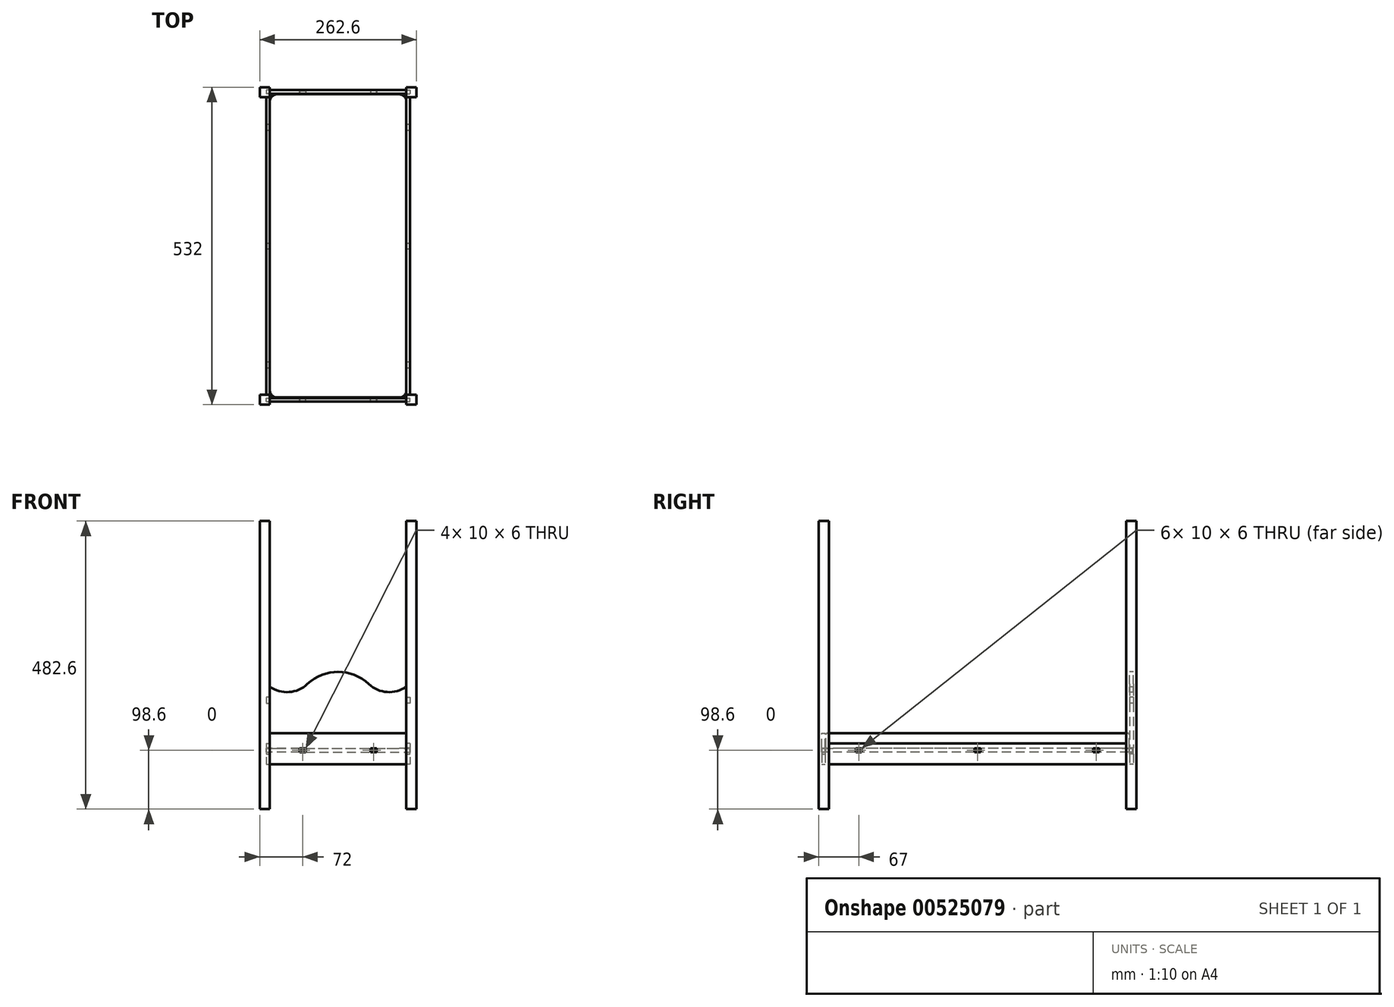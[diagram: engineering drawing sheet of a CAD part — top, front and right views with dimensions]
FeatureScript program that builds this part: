
annotation { "Feature Type Name" : "Feature", "Feature Type Description" : "" }
export const myFeature = defineFeature(function(context is Context, id is Id, definition is map)
    precondition{}
    {
        {
            var Q0;
            Q0=qCreatedBy(makeId("Top.planeOp"),FACE);
            cPlane(context, id + "F0", {"entities" : qUnion([Q0]), "cplaneType" : CPlaneType.OFFSET, "offset" : (5 * 25.4) * mm, "width" : 150 * mm, "height" : 150 * mm});
        }
        {
            var Q0;
            Q0=qCreatedBy(makeId("Top.planeOp"),FACE);
            cPlane(context, id + "F1", {"entities" : qUnion([Q0]), "cplaneType" : CPlaneType.OFFSET, "offset" : (4 * 25.4) * mm, "width" : 150 * mm, "height" : 150 * mm});
        }
        {
            var Q0;
            Q0=qCreatedBy(id+"F0.planeOp",FACE);
            var sketch = newSketch(context, id + "F2", { "sketchPlane" : qUnion([Q0])});
            skLineSegment(sketch, "E0.bottom", {"start": v(-114.3, 254) * mm, "end": v(114.3, 254) * mm});
            skLineSegment(sketch, "E0.top", {"start": v(-114.3, -254) * mm, "end": v(114.3, -254) * mm});
            skLineSegment(sketch, "E0.left", {"start": v(-114.3, 254) * mm, "end": v(-114.3, -254) * mm});
            skLineSegment(sketch, "E0.right", {"start": v(114.3, 254) * mm, "end": v(114.3, -254) * mm});
            skLineSegment(sketch, "E1", {"start": v(0, 66.41) * mm, "end": v(0, 0) * mm, "construction": true});
            skLineSegment(sketch, "E2", {"start": v(0, 0) * mm, "end": v(28.07, 0) * mm, "construction": true});
            skSolve(sketch);
        }
        {
            var Q0;
            Q0=qCreatedBy(id+"F1.planeOp",FACE);
            var sketch = newSketch(context, id + "F3", { "sketchPlane" : qUnion([Q0])});
            skLineSegment(sketch, "E3.0.0", {"start": v(-114.3, 254) * mm, "end": v(-114.3, 204) * mm});
            skLineSegment(sketch, "E3.0.1", {"start": v(-114.3, -254) * mm, "end": v(-64.3, -254) * mm});
            skLineSegment(sketch, "E3.0.2", {"start": v(114.3, -254) * mm, "end": v(114.3, -204) * mm});
            skLineSegment(sketch, "E3.0.3", {"start": v(114.3, 254) * mm, "end": v(64.3, 254) * mm});
            skLineSegment(sketch, "E4.0", {"start": v(0, 66.41) * mm, "end": v(0, 0) * mm, "construction": true});
            skPoint(sketch, "E5.0", {"position": v(14.03, 0) * mm});
            skLineSegment(sketch, "E6.bottom", {"start": v(-120.3, 5) * mm, "end": v(-114.3, 5) * mm});
            skLineSegment(sketch, "E6.top", {"start": v(-120.3, -5) * mm, "end": v(-114.3, -5) * mm});
            skLineSegment(sketch, "E6.left", {"start": v(-120.3, 5) * mm, "end": v(-120.3, -5) * mm});
            skLineSegment(sketch, "E6.right", {"start": v(120.3, 5) * mm, "end": v(120.3, -5) * mm});
            skPoint(sketch, "E7.0", {"position": v(14.03, 192.46) * mm});
            skLineSegment(sketch, "E8.bottom", {"start": v(-120.3, 204) * mm, "end": v(-114.3, 204) * mm});
            skLineSegment(sketch, "E8.top", {"start": v(-120.3, 194) * mm, "end": v(-114.3, 194) * mm});
            skLineSegment(sketch, "E8.left", {"start": v(-120.3, 204) * mm, "end": v(-120.3, 194) * mm});
            skLineSegment(sketch, "E8.right", {"start": v(120.3, 204) * mm, "end": v(120.3, 194) * mm});
            skLineSegment(sketch, "E9.MirrorCS", {"start": v(120.3, -204) * mm, "end": v(120.3, -194) * mm});
            skLineSegment(sketch, "E10.MirrorCS", {"start": v(-120.3, -204) * mm, "end": v(-120.3, -194) * mm});
            skLineSegment(sketch, "E11.MirrorCS", {"start": v(-120.3, -204) * mm, "end": v(-114.3, -204) * mm});
            skLineSegment(sketch, "E12.MirrorCS", {"start": v(-120.3, -194) * mm, "end": v(-114.3, -194) * mm});
            skPoint(sketch, "E13.MirrorP", {"position": v(14.03, -192.46) * mm});
            skLineSegment(sketch, "E14.trimOffspring", {"start": v(114.3, 204) * mm, "end": v(120.3, 204) * mm});
            skLineSegment(sketch, "E15.trimOffspring", {"start": v(114.3, 194) * mm, "end": v(120.3, 194) * mm});
            skLineSegment(sketch, "E16.trimOffspring", {"start": v(114.3, 5) * mm, "end": v(120.3, 5) * mm});
            skLineSegment(sketch, "E17.trimOffspring", {"start": v(114.3, -5) * mm, "end": v(120.3, -5) * mm});
            skLineSegment(sketch, "E18.trimOffspring", {"start": v(114.3, 5) * mm, "end": v(114.3, 194) * mm});
            skLineSegment(sketch, "E19.trimOffspring", {"start": v(-114.3, -5) * mm, "end": v(-114.3, -194) * mm});
            skLineSegment(sketch, "E20.trimOffspring", {"start": v(-114.3, 194) * mm, "end": v(-114.3, 5) * mm});
            skLineSegment(sketch, "E21.trimOffspring", {"start": v(114.3, 204) * mm, "end": v(114.3, 254) * mm});
            skLineSegment(sketch, "E22.trimOffspring", {"start": v(114.3, -194) * mm, "end": v(120.3, -194) * mm});
            skLineSegment(sketch, "E23.trimOffspring", {"start": v(114.3, -204) * mm, "end": v(120.3, -204) * mm});
            skLineSegment(sketch, "E24.trimOffspring", {"start": v(-114.3, -204) * mm, "end": v(-114.3, -254) * mm});
            skLineSegment(sketch, "E25.trimOffspring", {"start": v(114.3, -194) * mm, "end": v(114.3, -5) * mm});
            skLineSegment(sketch, "E26", {"start": v(-64.3, 254) * mm, "end": v(-64.3, 260) * mm});
            skLineSegment(sketch, "E27", {"start": v(-64.3, 260) * mm, "end": v(-54.3, 260) * mm});
            skLineSegment(sketch, "E28", {"start": v(-54.3, 260) * mm, "end": v(-54.3, 254) * mm});
            skLineSegment(sketch, "E29", {"start": v(64.3, 254) * mm, "end": v(64.3, 260) * mm});
            skLineSegment(sketch, "E30", {"start": v(64.3, 260) * mm, "end": v(54.3, 260) * mm});
            skLineSegment(sketch, "E31", {"start": v(54.3, 260) * mm, "end": v(54.3, 254) * mm});
            skLineSegment(sketch, "E32.trimOffspring", {"start": v(-64.3, 254) * mm, "end": v(-114.3, 254) * mm});
            skLineSegment(sketch, "E33.trimOffspring", {"start": v(54.3, 254) * mm, "end": v(-54.3, 254) * mm});
            skLineSegment(sketch, "E34.MirrorCS", {"start": v(-64.3, -254) * mm, "end": v(-64.3, -260) * mm});
            skLineSegment(sketch, "E35.MirrorCS", {"start": v(-54.3, -260) * mm, "end": v(-54.3, -254) * mm});
            skLineSegment(sketch, "E36.MirrorCS", {"start": v(64.3, -254) * mm, "end": v(64.3, -260) * mm});
            skLineSegment(sketch, "E37.MirrorCS", {"start": v(54.3, -260) * mm, "end": v(54.3, -254) * mm});
            skLineSegment(sketch, "E38.MirrorCS", {"start": v(64.3, -260) * mm, "end": v(54.3, -260) * mm});
            skLineSegment(sketch, "E39.MirrorCS", {"start": v(-64.3, -260) * mm, "end": v(-54.3, -260) * mm});
            skLineSegment(sketch, "E40.trimOffspring", {"start": v(-54.3, -254) * mm, "end": v(54.3, -254) * mm});
            skLineSegment(sketch, "E41.trimOffspring", {"start": v(64.3, -254) * mm, "end": v(114.3, -254) * mm});
            skSolve(sketch);
        }
        {
            var Q0;
            Q0=makeQuery(id+"F3.imprint","IMPRINT",FACE,{"disambiguationData":[TD([[makeQuery(id+"F3.imprint","IMPRINT",EDGE,{"derivedFrom":sQuery(id+"F3.wireOp",EDGE,"E3.0.0")}),1.0]])]});
            extrude(context, id + "F4", {"entities" : qUnion([Q0]), "oppositeDirection" : true, "depth" : 6 * mm, "offsetDistance" : 25 * mm});
        }
        {
            var Q0;
            Q0=makeQuery(id+"F2.imprint","IMPRINT",FACE,{"disambiguationData":[TD([[makeQuery(id+"F2.imprint","IMPRINT",EDGE,{"derivedFrom":sQuery(id+"F2.wireOp",EDGE,"E0.bottom")}),-1.0]])]});
            extrude(context, id + "F5", {"entities" : qUnion([Q0]), "oppositeDirection" : true, "depth" : 25 * mm, "offsetDistance" : 25 * mm});
        }
        {
            var Q0;
            Q0=makeQuery(id+"F5.opExtrude","SWEPT_EDGE",EDGE,{"disambiguationData":[OSD([sQuery(id+"F2.wireOp",EDGE,"E0.bottom"),sQuery(id+"F2.wireOp",EDGE,"E0.left")])]});
            var Q1;
            Q1=makeQuery(id+"F5.opExtrude","SWEPT_EDGE",EDGE,{"disambiguationData":[OSD([sQuery(id+"F2.wireOp",EDGE,"E0.top"),sQuery(id+"F2.wireOp",EDGE,"E0.left")])]});
            var Q2;
            Q2=makeQuery(id+"F5.opExtrude","SWEPT_EDGE",EDGE,{"disambiguationData":[OSD([sQuery(id+"F2.wireOp",EDGE,"E0.top"),sQuery(id+"F2.wireOp",EDGE,"E0.right")])]});
            var Q3;
            Q3=makeQuery(id+"F5.opExtrude","SWEPT_EDGE",EDGE,{"disambiguationData":[OSD([sQuery(id+"F2.wireOp",EDGE,"E0.bottom"),sQuery(id+"F2.wireOp",EDGE,"E0.right")])]});
            fillet(context, id + "F6", {"entities" : qUnion([Q0, Q1, Q2, Q3]), "radius" : 12 * mm, "tangentPropagation" : true, "allowEdgeOverflow" : false});
        }
        {
            var Q0;
            Q0=makeQuery(id+"F5.opExtrude","CAP_EDGE",EDGE,{"disambiguationData":[OSD([sQuery(id+"F2.wireOp",EDGE,"E0.right")])],"isStart":true});
            var Q1;
            Q1=makeQuery(id+"F5.opExtrude","CAP_EDGE",EDGE,{"disambiguationData":[OSD([sQuery(id+"F2.wireOp",EDGE,"E0.right")])],"isStart":false});
            fillet(context, id + "F7", {"entities" : qUnion([Q0, Q1]), "radius" : 2 * mm, "tangentPropagation" : true, "allowEdgeOverflow" : false});
        }
        {
            var Q0;
            Q0=qCreatedBy(makeId("Front.planeOp"),FACE);
            cPlane(context, id + "F8", {"entities" : qUnion([Q0]), "cplaneType" : CPlaneType.OFFSET, "offset" : 255 * mm, "oppositeDirection" : true, "width" : 150 * mm, "height" : 150 * mm});
        }
        {
            var Q0;
            Q0=qCreatedBy(id+"F8.planeOp",FACE);
            var sketch = newSketch(context, id + "F9", { "sketchPlane" : qUnion([Q0])});
            skLineSegment(sketch, "E42.top", {"start": v(114.3, 75) * mm, "end": v(-114.3, 75) * mm});
            skLineSegment(sketch, "E42.left", {"start": v(114.3, 205) * mm, "end": v(114.3, 187.5) * mm});
            skLineSegment(sketch, "E42.right", {"start": v(-114.3, 205) * mm, "end": v(-114.3, 187.5) * mm});
            skArc(sketch, "E43", {"start": v(51.41, 209.6) * mm, "mid": v(0, 230) * mm, "end": v(-51.41, 209.6) * mm});
            skArc(sketch, "E44", {"start": v(51.41, 209.6) * mm, "mid": v(82.04, 196.14) * mm, "end": v(114.3, 205) * mm});
            skArc(sketch, "E45.MirrorCS", {"start": v(-51.41, 209.6) * mm, "mid": v(-82.04, 196.14) * mm, "end": v(-114.3, 205) * mm});
            skLineSegment(sketch, "E46", {"start": v(51.46, 230) * mm, "end": v(-51.46, 230) * mm, "construction": true});
            skPoint(sketch, "E46.endSnap0", {"position": v(0, 230) * mm});
            skLineSegment(sketch, "E47", {"start": v(114.3, 140) * mm, "end": v(-114.3, 140) * mm, "construction": true});
            skLineSegment(sketch, "E48", {"start": v(114.3, 187.5) * mm, "end": v(120.3, 187.5) * mm});
            skLineSegment(sketch, "E49", {"start": v(120.3, 187.5) * mm, "end": v(120.3, 177.5) * mm});
            skLineSegment(sketch, "E50", {"start": v(120.3, 177.5) * mm, "end": v(114.3, 177.5) * mm});
            skLineSegment(sketch, "E51.MirrorCS", {"start": v(-120.3, 177.5) * mm, "end": v(-114.3, 177.5) * mm});
            skLineSegment(sketch, "E52.MirrorCS", {"start": v(-120.3, 187.5) * mm, "end": v(-120.3, 177.5) * mm});
            skLineSegment(sketch, "E53.MirrorCS", {"start": v(-114.3, 187.5) * mm, "end": v(-120.3, 187.5) * mm});
            skLineSegment(sketch, "E54.MirrorCS", {"start": v(-114.3, 92.5) * mm, "end": v(-120.3, 92.5) * mm});
            skLineSegment(sketch, "E55.MirrorCS", {"start": v(-120.3, 92.5) * mm, "end": v(-120.3, 102.5) * mm});
            skLineSegment(sketch, "E56.MirrorCS", {"start": v(-120.3, 102.5) * mm, "end": v(-114.3, 102.5) * mm});
            skLineSegment(sketch, "E57.MirrorCS", {"start": v(114.3, 92.5) * mm, "end": v(120.3, 92.5) * mm});
            skLineSegment(sketch, "E58.MirrorCS", {"start": v(120.3, 102.5) * mm, "end": v(114.3, 102.5) * mm});
            skLineSegment(sketch, "E59.MirrorCS", {"start": v(120.3, 92.5) * mm, "end": v(120.3, 102.5) * mm});
            skLineSegment(sketch, "E60.trimOffspring", {"start": v(114.3, 177.5) * mm, "end": v(114.3, 102.5) * mm});
            skLineSegment(sketch, "E61.trimOffspring", {"start": v(-114.3, 177.5) * mm, "end": v(-114.3, 102.5) * mm});
            skLineSegment(sketch, "E62.trimOffspring", {"start": v(-114.3, 92.5) * mm, "end": v(-114.3, 75) * mm});
            skLineSegment(sketch, "E63.trimOffspring", {"start": v(114.3, 92.5) * mm, "end": v(114.3, 75) * mm});
            skLineSegment(sketch, "E64.0.0", {"start": v(54.3, 101.6) * mm, "end": v(64.3, 101.6) * mm});
            skLineSegment(sketch, "E64.0.1", {"start": v(64.3, 101.6) * mm, "end": v(64.3, 95.6) * mm});
            skLineSegment(sketch, "E64.0.2", {"start": v(64.3, 95.6) * mm, "end": v(54.3, 95.6) * mm});
            skLineSegment(sketch, "E64.0.3", {"start": v(54.3, 95.6) * mm, "end": v(54.3, 101.6) * mm});
            skLineSegment(sketch, "E65.0.0", {"start": v(-64.3, 101.6) * mm, "end": v(-54.3, 101.6) * mm});
            skLineSegment(sketch, "E65.0.1", {"start": v(-54.3, 101.6) * mm, "end": v(-54.3, 95.6) * mm});
            skLineSegment(sketch, "E65.0.2", {"start": v(-54.3, 95.6) * mm, "end": v(-64.3, 95.6) * mm});
            skLineSegment(sketch, "E65.0.3", {"start": v(-64.3, 95.6) * mm, "end": v(-64.3, 101.6) * mm});
            skSolve(sketch);
        }
        {
            var Q0;
            Q0 = qSketchRegion(id + "F9", true);
            extrude(context, id + "F10", {"entities" : qUnion([Q0]), "oppositeDirection" : true, "depth" : 6 * mm, "offsetDistance" : 25 * mm});
        }
        {
            var Q0;
            Q0=qCreatedBy(makeId("Front.planeOp"),FACE);
            cPlane(context, id + "F11", {"entities" : qUnion([Q0]), "cplaneType" : CPlaneType.OFFSET, "offset" : 255 * mm, "width" : 150 * mm, "height" : 150 * mm});
        }
        {
            var Q0;
            Q0=qCreatedBy(id+"F11.planeOp",FACE);
            var sketch = newSketch(context, id + "F12", { "sketchPlane" : qUnion([Q0])});
            skLineSegment(sketch, "E66.0", {"start": v(-114.3, 92.5) * mm, "end": v(-114.3, 75) * mm});
            skLineSegment(sketch, "E67", {"start": v(-114.3, 127.27) * mm, "end": v(114.3, 127.27) * mm});
            skLineSegment(sketch, "E68.0.10", {"start": v(-114.3, 102.5) * mm, "end": v(-120.3, 102.5) * mm});
            skLineSegment(sketch, "E68.0.11", {"start": v(-120.3, 102.5) * mm, "end": v(-120.3, 92.5) * mm});
            skLineSegment(sketch, "E68.0.12", {"start": v(-120.3, 92.5) * mm, "end": v(-114.3, 92.5) * mm});
            skLineSegment(sketch, "E68.0.14", {"start": v(-114.3, 75) * mm, "end": v(114.3, 75) * mm});
            skLineSegment(sketch, "E68.0.15", {"start": v(114.3, 75) * mm, "end": v(114.3, 92.5) * mm});
            skLineSegment(sketch, "E68.0.16", {"start": v(114.3, 92.5) * mm, "end": v(120.3, 92.5) * mm});
            skLineSegment(sketch, "E68.0.17", {"start": v(120.3, 92.5) * mm, "end": v(120.3, 102.5) * mm});
            skLineSegment(sketch, "E68.0.18", {"start": v(120.3, 102.5) * mm, "end": v(114.3, 102.5) * mm});
            skLineSegment(sketch, "E68.0.19", {"start": v(114.3, 102.5) * mm, "end": v(114.3, 127.27) * mm});
            skLineSegment(sketch, "E69.0", {"start": v(-114.3, 127.27) * mm, "end": v(-114.3, 102.5) * mm});
            skPoint(sketch, "E70.orphan", {"position": v(-114.3, 177.5) * mm});
            skLineSegment(sketch, "E71.0.0", {"start": v(-54.3, 101.6) * mm, "end": v(-64.3, 101.6) * mm});
            skLineSegment(sketch, "E71.0.1", {"start": v(-64.3, 101.6) * mm, "end": v(-64.3, 95.6) * mm});
            skLineSegment(sketch, "E71.0.2", {"start": v(-64.3, 95.6) * mm, "end": v(-54.3, 95.6) * mm});
            skLineSegment(sketch, "E71.0.3", {"start": v(-54.3, 95.6) * mm, "end": v(-54.3, 101.6) * mm});
            skLineSegment(sketch, "E72.0.0", {"start": v(64.3, 101.6) * mm, "end": v(54.3, 101.6) * mm});
            skLineSegment(sketch, "E72.0.1", {"start": v(54.3, 101.6) * mm, "end": v(54.3, 95.6) * mm});
            skLineSegment(sketch, "E72.0.2", {"start": v(54.3, 95.6) * mm, "end": v(64.3, 95.6) * mm});
            skLineSegment(sketch, "E72.0.3", {"start": v(64.3, 95.6) * mm, "end": v(64.3, 101.6) * mm});
            skSolve(sketch);
        }
        {
            var Q0;
            Q0 = qSketchRegion(id + "F12", true);
            extrude(context, id + "F13", {"entities" : qUnion([Q0]), "depth" : 6 * mm, "offsetDistance" : 25 * mm});
        }
        {
            var Q0;
            Q0=qCreatedBy(makeId("Right.planeOp"),FACE);
            cPlane(context, id + "F14", {"entities" : qUnion([Q0]), "cplaneType" : CPlaneType.OFFSET, "offset" : (4.5 * 25.4) * mm, "oppositeDirection" : true, "width" : 150 * mm, "height" : 150 * mm});
        }
        {
            var Q0;
            Q0=qCreatedBy(id+"F14.planeOp",FACE);
            var sketch = newSketch(context, id + "F15", { "sketchPlane" : qUnion([Q0])});
            skLineSegment(sketch, "E73", {"start": v(249, 110) * mm, "end": v(-249, 110) * mm});
            skLineSegment(sketch, "E74.0", {"start": v(249, 75) * mm, "end": v(-249, 75) * mm});
            skLineSegment(sketch, "E75.0.0", {"start": v(-204, 101.6) * mm, "end": v(-194, 101.6) * mm});
            skLineSegment(sketch, "E75.0.1", {"start": v(-194, 101.6) * mm, "end": v(-194, 95.6) * mm});
            skLineSegment(sketch, "E75.0.2", {"start": v(-194, 95.6) * mm, "end": v(-204, 95.6) * mm});
            skLineSegment(sketch, "E75.0.3", {"start": v(-204, 95.6) * mm, "end": v(-204, 101.6) * mm});
            skLineSegment(sketch, "E76.0.0", {"start": v(-5, 101.6) * mm, "end": v(5, 101.6) * mm});
            skLineSegment(sketch, "E76.0.1", {"start": v(5, 101.6) * mm, "end": v(5, 95.6) * mm});
            skLineSegment(sketch, "E76.0.2", {"start": v(5, 95.6) * mm, "end": v(-5, 95.6) * mm});
            skLineSegment(sketch, "E76.0.3", {"start": v(-5, 95.6) * mm, "end": v(-5, 101.6) * mm});
            skLineSegment(sketch, "E77.0.0", {"start": v(194, 101.6) * mm, "end": v(204, 101.6) * mm});
            skLineSegment(sketch, "E77.0.1", {"start": v(204, 101.6) * mm, "end": v(204, 95.6) * mm});
            skLineSegment(sketch, "E77.0.2", {"start": v(204, 95.6) * mm, "end": v(194, 95.6) * mm});
            skLineSegment(sketch, "E77.0.3", {"start": v(194, 95.6) * mm, "end": v(194, 101.6) * mm});
            skLineSegment(sketch, "E78", {"start": v(-249, 110) * mm, "end": v(-249, 75) * mm});
            skPoint(sketch, "E79.0.end.orphan", {"position": v(-261, 75) * mm});
            skLineSegment(sketch, "E80", {"start": v(249, 110) * mm, "end": v(249, 75) * mm});
            skPoint(sketch, "E81.orphan", {"position": v(261, 75) * mm});
            skSolve(sketch);
        }
        {
            var Q0;
            Q0 = qSketchRegion(id + "F15", true);
            extrude(context, id + "F16", {"entities" : qUnion([Q0]), "oppositeDirection" : true, "depth" : 6 * mm, "offsetDistance" : 25 * mm});
        }
        {
            var Q0;
            Q0=makeQuery(id+"F16.opExtrude","SWEPT_BODY",BODY,{"disambiguationData":[OSD([sQuery(id+"F15.wireOp",EDGE,"E73"),sQuery(id+"F15.wireOp",EDGE,"3c840a2c-036b-4376-a69c-f623c423800d.0"),sQuery(id+"F15.wireOp",EDGE,"E74.0"),sQuery(id+"F15.wireOp",EDGE,"E75.0.0"),sQuery(id+"F15.wireOp",EDGE,"E75.0.1"),sQuery(id+"F15.wireOp",EDGE,"E75.0.2"),sQuery(id+"F15.wireOp",EDGE,"E75.0.3"),sQuery(id+"F15.wireOp",EDGE,"E76.0.0"),sQuery(id+"F15.wireOp",EDGE,"E76.0.1"),sQuery(id+"F15.wireOp",EDGE,"E76.0.2"),sQuery(id+"F15.wireOp",EDGE,"E76.0.3"),sQuery(id+"F15.wireOp",EDGE,"E77.0.0"),sQuery(id+"F15.wireOp",EDGE,"E77.0.1"),sQuery(id+"F15.wireOp",EDGE,"E77.0.2"),sQuery(id+"F15.wireOp",EDGE,"E77.0.3"),sQuery(id+"F15.wireOp",EDGE,"E79.0")])]});
            var Q1;
            Q1=qCreatedBy(makeId("Right.planeOp"),FACE);
            mirror(context, id + "F17", {"entities" : qUnion([Q0]), "mirrorPlane" : qUnion([Q1])});
        }
        {
            var Q0;
            Q0=qCreatedBy(makeId("Top.planeOp"),FACE);
            var sketch = newSketch(context, id + "F18", { "sketchPlane" : qUnion([Q0])});
            skLineSegment(sketch, "E82.bottom", {"start": v(-114.3, 266) * mm, "end": v(-131.3, 266) * mm});
            skLineSegment(sketch, "E82.top", {"start": v(-114.3, 249) * mm, "end": v(-131.3, 249) * mm});
            skLineSegment(sketch, "E82.left", {"start": v(-114.3, 266) * mm, "end": v(-114.3, 249) * mm});
            skLineSegment(sketch, "E82.right", {"start": v(-131.3, 266) * mm, "end": v(-131.3, 249) * mm});
            skSolve(sketch);
        }
        {
            var Q0;
            Q0=makeQuery(id+"F18.imprint","IMPRINT",FACE,{"disambiguationData":[TD([[makeQuery(id+"F18.imprint","IMPRINT",EDGE,{"derivedFrom":sQuery(id+"F18.wireOp",EDGE,"E82.bottom")}),1.0]])]});
            extrude(context, id + "F19", {"entities" : qUnion([Q0]), "depth" : (19 * 25.4) * mm, "offsetDistance" : 25 * mm});
        }
        {
            var Q0;
            Q0=makeQuery(id+"F19.opExtrude","SWEPT_BODY",BODY,{"disambiguationData":[OSD([sQuery(id+"F18.wireOp",EDGE,"E82.bottom"),sQuery(id+"F18.wireOp",EDGE,"E82.top"),sQuery(id+"F18.wireOp",EDGE,"E82.left"),sQuery(id+"F18.wireOp",EDGE,"E82.right")])]});
            var Q1;
            Q1=qCreatedBy(makeId("Right.planeOp"),FACE);
            mirror(context, id + "F20", {"entities" : qUnion([Q0]), "mirrorPlane" : qUnion([Q1])});
        }
        {
            var Q0;
            Q0=makeQuery(id+"F19.opExtrude","SWEPT_BODY",BODY,{"disambiguationData":[OSD([sQuery(id+"F18.wireOp",EDGE,"E82.bottom"),sQuery(id+"F18.wireOp",EDGE,"E82.top"),sQuery(id+"F18.wireOp",EDGE,"E82.left"),sQuery(id+"F18.wireOp",EDGE,"E82.right")])]});
            var Q1;
            Q1=makeQuery(id+"F20.opPattern","COPY",BODY,{"derivedFrom":makeQuery(id+"F19.opExtrude","SWEPT_BODY",BODY,{"disambiguationData":[OSD([sQuery(id+"F18.wireOp",EDGE,"E82.bottom"),sQuery(id+"F18.wireOp",EDGE,"E82.top"),sQuery(id+"F18.wireOp",EDGE,"E82.left"),sQuery(id+"F18.wireOp",EDGE,"E82.right")])]}),"instanceName":"1"});
            var Q2;
            Q2=qCreatedBy(makeId("Front.planeOp"),FACE);
            mirror(context, id + "F21", {"entities" : qUnion([Q0, Q1]), "mirrorPlane" : qUnion([Q2])});
        }
    });
